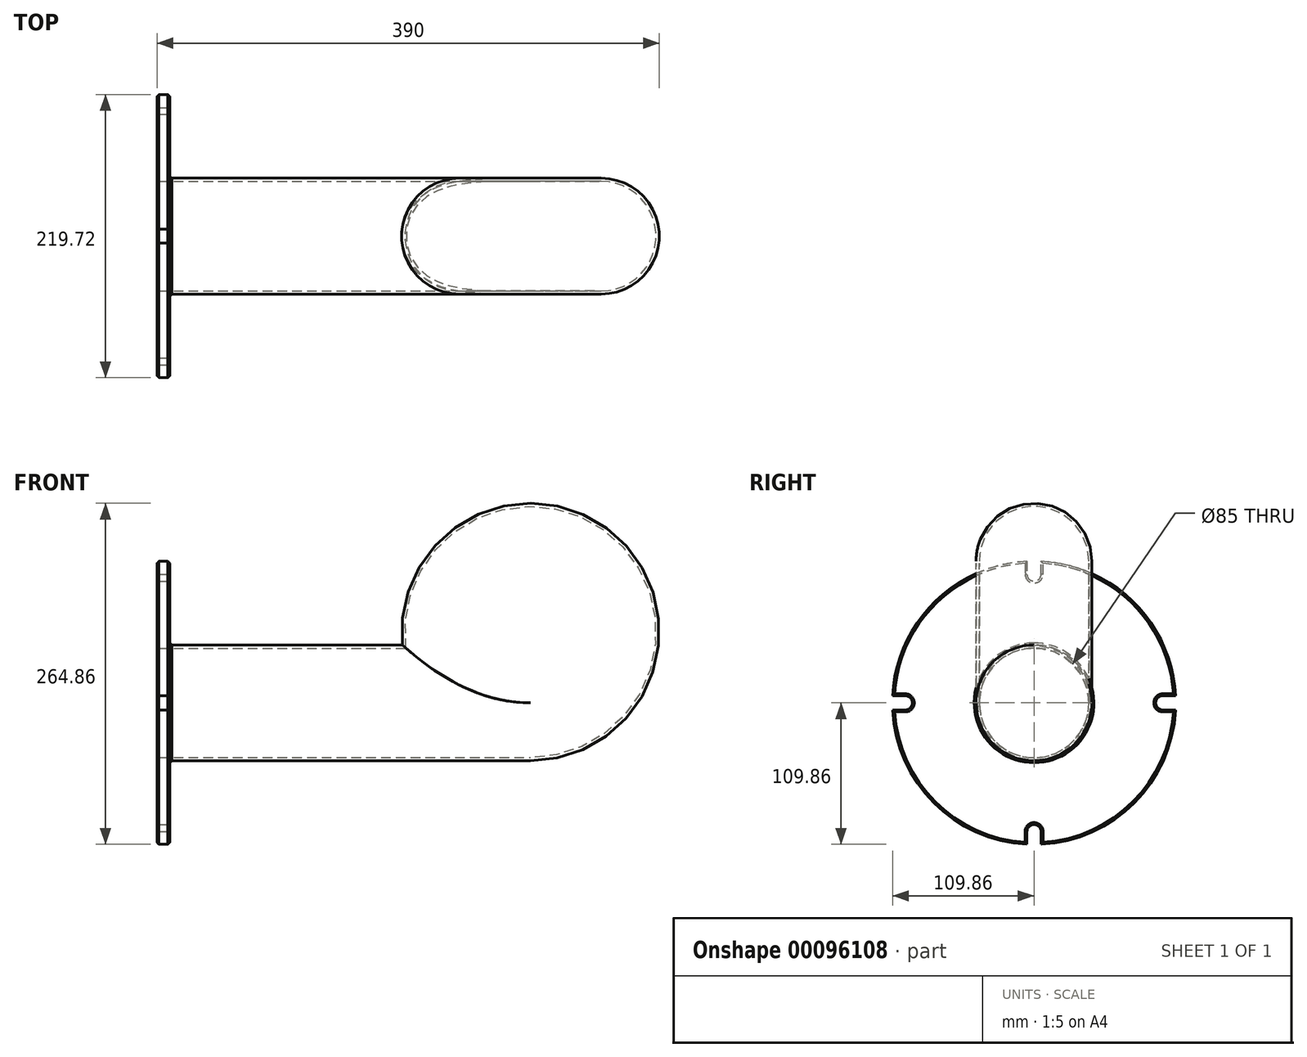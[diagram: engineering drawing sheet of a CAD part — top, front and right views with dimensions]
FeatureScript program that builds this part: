
annotation { "Feature Type Name" : "Feature", "Feature Type Description" : "" }
export const myFeature = defineFeature(function(context is Context, id is Id, definition is map)
    precondition{}
    {
        {
            var Q0;
            Q0=qCreatedBy(makeId("Front.planeOp"),FACE);
            var sketch = newSketch(context, id + "F0", { "sketchPlane" : qUnion([Q0])});
            skCircle(sketch, "E0", {"center": v(0, 0) * mm, "radius": 100 * mm});
            skLineSegment(sketch, "E1.bottom", {"start": v(0, -100) * mm, "end": v(-280, -100) * mm});
            skLineSegment(sketch, "E1.top", {"start": v(0, -10) * mm, "end": v(-280, -10) * mm});
            skLineSegment(sketch, "E1.left", {"start": v(0, -100) * mm, "end": v(0, -10) * mm});
            skLineSegment(sketch, "E1.right", {"start": v(-280, -100) * mm, "end": v(-280, -10) * mm});
            skSolve(sketch);
        }
        {
            var Q0;
            Q0 = qSketchRegion(id + "F0", true);
            var Q1;
            {var subQ0=sQuery(id+"F0.wireOp",EDGE,"E1.bottom");Q1=makeQuery(id+"F0.imprint","IMPRINT",FACE,{"disambiguationData":[TD([[makeQuery(id+"F0.imprint","IMPRINT",EDGE,{"derivedFrom":subQ0}),-1.0]])]});}
            extrude(context, id + "F1", {"entities" : qUnion([Q0, Q1]), "endBound" : BoundingType.SYMMETRIC, "depth" : 90 * mm});
        }
        {
            var Q0;
            Q0=makeQuery(id+"F1.opExtrude","CAP_EDGE",EDGE,{"disambiguationData":[OSD([sQuery(id+"F0.wireOp",EDGE,"E1.top")])],"isStart":false});
            var Q1;
            Q1=makeQuery(id+"F1.opExtrude","CAP_EDGE",EDGE,{"disambiguationData":[OSD([sQuery(id+"F0.wireOp",EDGE,"E1.top")])],"isStart":true});
            var Q2;
            Q2=makeQuery(id+"F1.opExtrude","CAP_EDGE",EDGE,{"disambiguationData":[OSD([sQuery(id+"F0.wireOp",EDGE,"E1.bottom")])],"isStart":true});
            var Q3;
            Q3=makeQuery(id+"F1.opExtrude","CAP_EDGE",EDGE,{"disambiguationData":[OSD([sQuery(id+"F0.wireOp",EDGE,"E1.bottom")])],"isStart":false});
            fillet(context, id + "F2", {"entities" : qUnion([Q0, Q1, Q2, Q3]), "radius" : 45 * mm, "tangentPropagation" : true, "allowEdgeOverflow" : false});
        }
        {
            var Q0;
            Q0=makeQuery(id+"F1.opExtrude","SWEPT_FACE",FACE,{"disambiguationData":[OSD([sQuery(id+"F0.wireOp",EDGE,"E1.right")])]});
            var sketch = newSketch(context, id + "F3", { "sketchPlane" : qUnion([Q0])});
            skArc(sketch, "E2", {"start": v(-5.5, 54.86) * mm, "mid": v(-77.78, 22.78) * mm, "end": v(-109.86, -49.5) * mm});
            skArc(sketch, "E3", {"start": v(-5.5, 45.15) * mm, "mid": v(0, 39.5) * mm, "end": v(5.5, 45.15) * mm});
            skArc(sketch, "E4", {"start": v(-100.15, -60.5) * mm, "mid": v(-94.5, -55) * mm, "end": v(-100.15, -49.5) * mm});
            skArc(sketch, "E5", {"start": v(100.15, -49.5) * mm, "mid": v(94.5, -55) * mm, "end": v(100.15, -60.5) * mm});
            skArc(sketch, "E6", {"start": v(5.5, -155.15) * mm, "mid": v(0, -149.5) * mm, "end": v(-5.5, -155.15) * mm});
            skLineSegment(sketch, "E7", {"start": v(99.85, -49.5) * mm, "end": v(109.86, -49.5) * mm});
            skLineSegment(sketch, "E8", {"start": v(99.85, -60.5) * mm, "end": v(109.86, -60.5) * mm});
            skLineSegment(sketch, "E9", {"start": v(-5.5, -154.85) * mm, "end": v(-5.5, -164.86) * mm});
            skLineSegment(sketch, "E10", {"start": v(5.5, -154.85) * mm, "end": v(5.5, -164.86) * mm});
            skLineSegment(sketch, "E11", {"start": v(-99.85, -60.5) * mm, "end": v(-109.86, -60.5) * mm});
            skLineSegment(sketch, "E12", {"start": v(-99.85, -49.5) * mm, "end": v(-109.86, -49.5) * mm});
            skLineSegment(sketch, "E13", {"start": v(5.5, 44.85) * mm, "end": v(5.5, 54.86) * mm});
            skLineSegment(sketch, "E14", {"start": v(-5.5, 44.85) * mm, "end": v(-5.5, 54.86) * mm});
            skArc(sketch, "E15.trimOffspring", {"start": v(109.86, -49.5) * mm, "mid": v(77.78, 22.78) * mm, "end": v(5.5, 54.86) * mm});
            skArc(sketch, "E16.trimOffspring", {"start": v(5.5, -164.86) * mm, "mid": v(77.78, -132.78) * mm, "end": v(109.86, -60.5) * mm});
            skArc(sketch, "E17.trimOffspring", {"start": v(-109.86, -60.5) * mm, "mid": v(-77.78, -132.78) * mm, "end": v(-5.5, -164.86) * mm});
            skCircle(sketch, "E18", {"center": v(0, -55) * mm, "radius": 42.5 * mm});
            skSolve(sketch);
        }
        {
            var Q0;
            Q0=makeQuery(id+"F1.opExtrude","SWEPT_FACE",FACE,{"disambiguationData":[OSD([sQuery(id+"F0.wireOp",EDGE,"E1.right")])]});
            shell(context, id + "F4", {"entities" : qUnion([Q0]), "thickness" : 2.5 * mm});
        }
        {
            var Q0;
            Q0 = qSketchRegion(id + "F3", true);
            var Q1;
            {var subQ1=sQuery(id+"F3.wireOp",EDGE,"E2");Q1=makeQuery(id+"F3.imprint","IMPRINT",FACE,{"disambiguationData":[TD([[makeQuery(id+"F3.imprint","IMPRINT",EDGE,{"derivedFrom":subQ1}),1.0]])]});}
            extrude(context, id + "F5", {"entities" : qUnion([Q0, Q1]), "operationType" : NewBodyOperationType.ADD, "depth" : 10 * mm});
        }
        {
            var Q0;
            Q0=makeQuery(id+"F5.opExtrude","CAP_FACE",FACE,{"disambiguationData":[OSD([sQuery(id+"F3.wireOp",EDGE,"E2"),sQuery(id+"F3.wireOp",EDGE,"E3"),sQuery(id+"F3.wireOp",EDGE,"E4"),sQuery(id+"F3.wireOp",EDGE,"E5"),sQuery(id+"F3.wireOp",EDGE,"E6"),sQuery(id+"F3.wireOp",EDGE,"E7"),sQuery(id+"F3.wireOp",EDGE,"E8"),sQuery(id+"F3.wireOp",EDGE,"E9"),sQuery(id+"F3.wireOp",EDGE,"E10"),sQuery(id+"F3.wireOp",EDGE,"E11"),sQuery(id+"F3.wireOp",EDGE,"E12"),sQuery(id+"F3.wireOp",EDGE,"E13"),sQuery(id+"F3.wireOp",EDGE,"E14"),sQuery(id+"F3.wireOp",EDGE,"E15.trimOffspring"),sQuery(id+"F3.wireOp",EDGE,"E16.trimOffspring"),sQuery(id+"F3.wireOp",EDGE,"E17.trimOffspring"),sQuery(id+"F3.wireOp",EDGE,"E18")])],"isStart":false});
            var Q1;
            Q1=makeQuery(id+"F5.opExtrude","CAP_FACE",FACE,{"disambiguationData":[OSD([sQuery(id+"F3.wireOp",EDGE,"E2"),sQuery(id+"F3.wireOp",EDGE,"E3"),sQuery(id+"F3.wireOp",EDGE,"E4"),sQuery(id+"F3.wireOp",EDGE,"E5"),sQuery(id+"F3.wireOp",EDGE,"E6"),sQuery(id+"F3.wireOp",EDGE,"E7"),sQuery(id+"F3.wireOp",EDGE,"E8"),sQuery(id+"F3.wireOp",EDGE,"E9"),sQuery(id+"F3.wireOp",EDGE,"E10"),sQuery(id+"F3.wireOp",EDGE,"E11"),sQuery(id+"F3.wireOp",EDGE,"E12"),sQuery(id+"F3.wireOp",EDGE,"E13"),sQuery(id+"F3.wireOp",EDGE,"E14"),sQuery(id+"F3.wireOp",EDGE,"E15.trimOffspring"),sQuery(id+"F3.wireOp",EDGE,"E16.trimOffspring"),sQuery(id+"F3.wireOp",EDGE,"E17.trimOffspring"),sQuery(id+"F3.wireOp",EDGE,"E18")])],"isStart":true});
            chamfer(context, id + "F6", {"entities" : qUnion([Q0, Q1]), "width" : 1.5 * mm, "tangentPropagation" : true});
        }
    });
